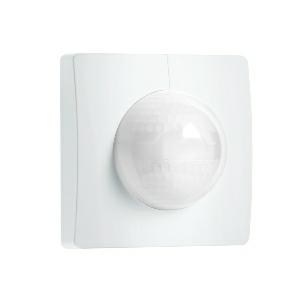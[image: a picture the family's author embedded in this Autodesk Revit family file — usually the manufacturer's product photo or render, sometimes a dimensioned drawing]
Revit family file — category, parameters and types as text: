
# Revit family: is_3180_055738
name_source: partatom
category: Elektroinstallationen
revit_build: Autodesk Revit 2016 (Build: 20190508_0715(x64)
units: mm (PartAtom-declared; Revit-internal decimal feet)

## family parameters
Basisbauteil = Fläche
Beim Laden mit Abzugskörper schneiden = Nein
Bemaßung runder Anschluss = Durchmesser verwenden
Beschriftungsausrichtung beibehalten = Nein
Gemeinsam genutzt = Nein
Raumberechnungspunkt = Nein
Teiletyp = Normal

## types (1)
- IS 3180
    Apparent Load = 0 VA
    Beschreibung = Type: Motion detectors; Dimensions (L x W x H): 78 x 94 x 94 mm; Mains power supply: 220 – 240 V / 50 – 60 Hz; Sensor Technology: passive infrared; Application, place: Indoors; Application, room: corridor / aisle, function room / ancillary room, stairwell, multi-storey / underground car park, outdoors, all round the building, courtyard & driveway, Indoors; Installation site: wall, corner; Installation: Concealed wiring; Switching zones: 448 switching zones; Electronic scalability: No; Mechanical scalability: No; Mounting height: 1,80 – 2,50 m; Optimum mounting height: 2 m; Detection angle: 180 °; Angle of aperture: 90 °; Sneak-by guard: Yes; Capability of masking out individual segments: Yes; Reach, radial: r = 3 m (14 m²) / r = 4 m (25 m²); Reach, tangential: r = 6 m (57 m²) / r = 20 m (628 m²); Twilight setting TEACH: Yes; Twilight setting: 2 – 1000 lx; Time setting: 5 sec – 15 min; Control output, Dali: Broadcast 1x30 electronic ballasts; Constant-lighting control: Yes; Basic light level function: Yes; Basic light level function in per cent: 10 – 50 %; Basic light level function time: 1-30 min, all night; Basic light level function percentage, from: 10 %; Basic light level function percentage, up to: 50 %; Functions: Normal / test mode, Manual ON / ON-OFF, Constant-lighting control ON-OFF; Settings via: Remote control, Potentiometers, Smart Remote; With remote control: No; Interconnection: Yes; IP-rating: IP20; Material: Plastic; Ambient temperature: -20 – 50 °C; Colour: white; Colour, RAL: 9003; Manufacturer's Warranty: 5 years; Version: DALI-2 Application Controller - concealed, sq.; PU1, EAN: 4007841055738
    Height = 94 mm  [stored 0.308399 ft]
    Hersteller = Steinel
    Length = 78 mm  [stored 0.255906 ft]
    Maximum range = 22.153 m
    ModVariant = Nein
    Modell = 055738
    Mounting Type = Recessed
    Number of Poles = 1
    OnlyDefault = Ja
    Power Factor = 1
    Product Name = IS 3180
    Product group = Sensor-switched indoor light
    ProductGroupID = 30
    Protection Class = Protection class
    Protection Degree = IP 20
    RlxData = <blob elided: 168261 chars, md5=b4e303ba>
    Sensor characteristics = Semi circular 145°-300°
    Sensor type = Passive (infrared)
    SensorDataFile = <blob elided: 5082 chars, md5=d953030a>
    Type of entry = Motion
    Typenbild = produkt1_055738.jpg
    Typenkommentare = Product without accessories
    URL = http://relux.com
    VarID = ---
    Voltage = 0 V
    Vorgabe-Ansicht = 1800 mm
    Weight = 0.00 kg
    Width = 94 mm  [stored 0.308399 ft]

note: [stored X ft] marks values corroborated as IEEE doubles in the binary element streams (Revit-internal decimal feet)

## geometry (parser evidence)
native form markers: Sweep x14
no freeform markers — native parametric forms only
